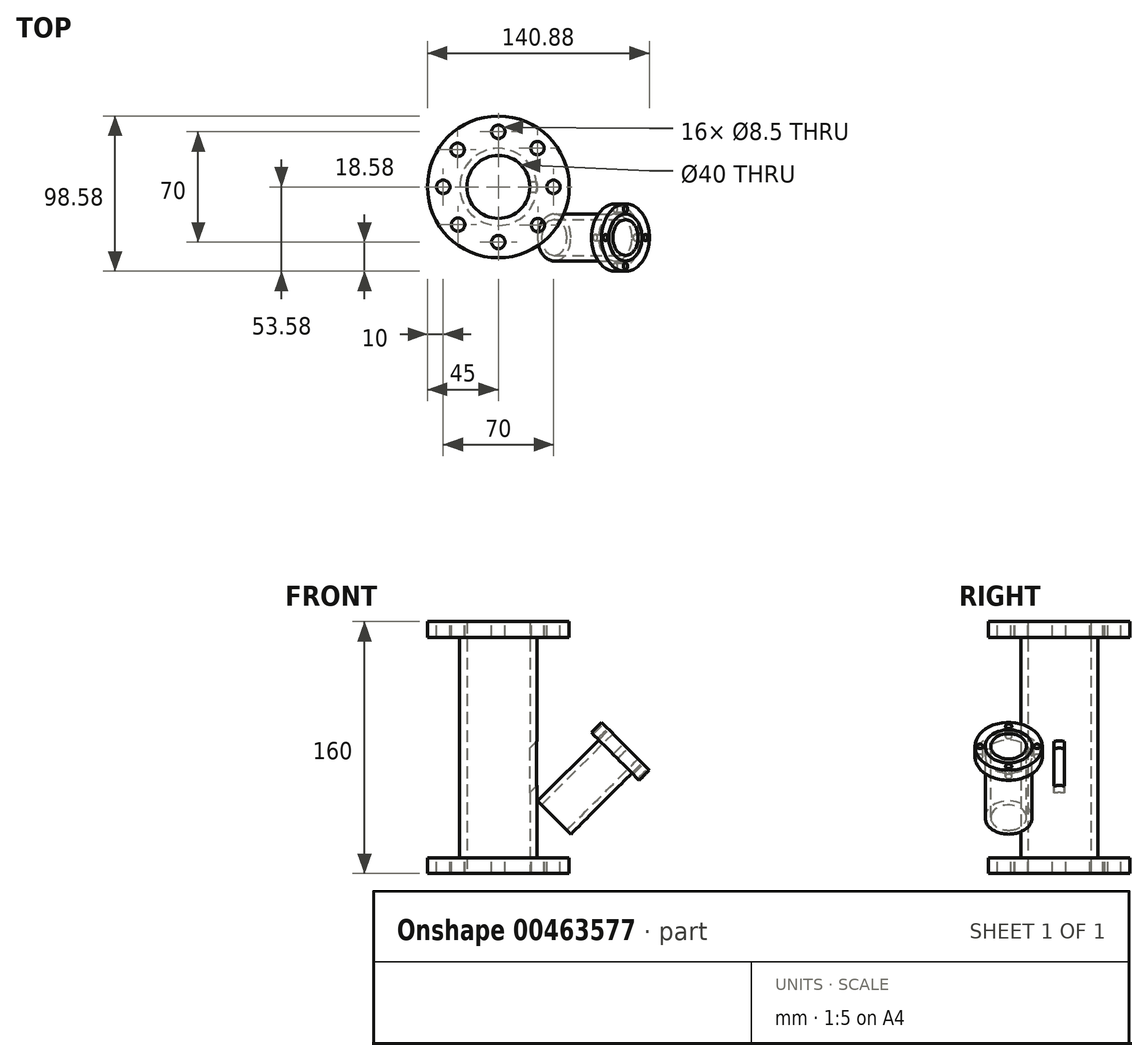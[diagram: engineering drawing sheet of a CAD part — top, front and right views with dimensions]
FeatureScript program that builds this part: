
annotation { "Feature Type Name" : "Feature", "Feature Type Description" : "" }
export const myFeature = defineFeature(function(context is Context, id is Id, definition is map)
    precondition{}
    {
        {
            var Q0;
            Q0=qCreatedBy(makeId("Top.planeOp"),FACE);
            var sketch = newSketch(context, id + "F0", { "sketchPlane" : qUnion([Q0])});
            skCircle(sketch, "E0", {"center": v(0, 0) * mm, "radius": 45 * mm});
            skCircle(sketch, "E1", {"center": v(0, 0) * mm, "radius": 20 * mm});
            skCircle(sketch, "E2", {"center": v(0, 0) * mm, "radius": 24.5 * mm});
            skSolve(sketch);
        }
        {
            var Q0;
            Q0=makeQuery(id+"F0.imprint","IMPRINT",FACE,{"disambiguationData":[TD([[makeQuery(id+"F0.imprint","IMPRINT",EDGE,{"derivedFrom":sQuery(id+"F0.wireOp",EDGE,"E0")}),1.0]])]});
            extrude(context, id + "F1", {"entities" : qUnion([Q0]), "depth" : 10 * mm});
        }
        {
            var Q0;
            Q0=makeQuery(id+"F0.imprint","IMPRINT",FACE,{"disambiguationData":[TD([[makeQuery(id+"F0.imprint","IMPRINT",EDGE,{"derivedFrom":sQuery(id+"F0.wireOp",EDGE,"E1")}),-1.0]])]});
            extrude(context, id + "F2", {"entities" : qUnion([Q0]), "operationType" : NewBodyOperationType.ADD, "depth" : 160 * mm});
        }
        {
            var Q0;
            Q0=makeQuery(id+"F2.opExtrude","CAP_FACE",FACE,{"disambiguationData":[OSD([sQuery(id+"F0.wireOp",EDGE,"E1"),sQuery(id+"F0.wireOp",EDGE,"E2")])],"isStart":false});
            var sketch = newSketch(context, id + "F3", { "sketchPlane" : qUnion([Q0])});
            skCircle(sketch, "E3", {"center": v(0, 0) * mm, "radius": 45 * mm});
            skSolve(sketch);
        }
        {
            var Q0;
            Q0=makeQuery(id+"F3.imprint","IMPRINT",FACE,{"disambiguationData":[TD([[makeQuery(id+"F3.imprint","IMPRINT",EDGE,{"derivedFrom":sQuery(id+"F3.wireOp",EDGE,"E3")}),1.0]])]});
            extrude(context, id + "F4", {"entities" : qUnion([Q0]), "operationType" : NewBodyOperationType.ADD, "oppositeDirection" : true, "depth" : 10 * mm});
        }
        {
            var Q0;
            {var subQ0=sQuery(id+"F0.wireOp",EDGE,"E2");Q0=makeQuery(id+"F4.boolean.opBoolean","MERGE",FACE,{"derivedFrom":[makeQuery(id+"F2.opExtrude","CAP_FACE",FACE,{"disambiguationData":[OSD([sQuery(id+"F0.wireOp",EDGE,"E1"),subQ0])],"isStart":false}),makeQuery(id+"F4.opExtrude","CAP_FACE",FACE,{"disambiguationData":[OSD([subQ0,sQuery(id+"F3.wireOp",EDGE,"E3")])],"isStart":true})]});}
            var sketch = newSketch(context, id + "F5", { "sketchPlane" : qUnion([Q0])});
            skCircle(sketch, "E4", {"center": v(0, 35) * mm, "radius": 4.25 * mm});
            skCircle(sketch, "E5", {"center": v(35, 0) * mm, "radius": 4.25 * mm});
            skCircle(sketch, "E6", {"center": v(0, -35) * mm, "radius": 4.25 * mm});
            skCircle(sketch, "E7", {"center": v(-35, 0) * mm, "radius": 4.25 * mm});
            skCircle(sketch, "E8", {"center": v(-25.85, 23.6) * mm, "radius": 4.25 * mm});
            skCircle(sketch, "E9", {"center": v(24.86, 24.63) * mm, "radius": 4.25 * mm});
            skCircle(sketch, "E10", {"center": v(25.17, -24.32) * mm, "radius": 4.25 * mm});
            skCircle(sketch, "E11", {"center": v(-25.53, -23.94) * mm, "radius": 4.25 * mm});
            skSolve(sketch);
        }
        {
            var Q0;
            Q0=makeQuery(id+"F5.imprint","IMPRINT",FACE,{"disambiguationData":[TD([[makeQuery(id+"F5.imprint","IMPRINT",EDGE,{"derivedFrom":sQuery(id+"F5.wireOp",EDGE,"E8")}),1.0]])]});
            var Q1;
            Q1=makeQuery(id+"F5.imprint","IMPRINT",FACE,{"disambiguationData":[TD([[makeQuery(id+"F5.imprint","IMPRINT",EDGE,{"derivedFrom":sQuery(id+"F5.wireOp",EDGE,"E4")}),1.0]])]});
            var Q2;
            Q2=makeQuery(id+"F5.imprint","IMPRINT",FACE,{"disambiguationData":[TD([[makeQuery(id+"F5.imprint","IMPRINT",EDGE,{"derivedFrom":sQuery(id+"F5.wireOp",EDGE,"E7")}),1.0]])]});
            var Q3;
            Q3=makeQuery(id+"F5.imprint","IMPRINT",FACE,{"disambiguationData":[TD([[makeQuery(id+"F5.imprint","IMPRINT",EDGE,{"derivedFrom":sQuery(id+"F5.wireOp",EDGE,"E11")}),1.0]])]});
            var Q4;
            Q4=makeQuery(id+"F5.imprint","IMPRINT",FACE,{"disambiguationData":[TD([[makeQuery(id+"F5.imprint","IMPRINT",EDGE,{"derivedFrom":sQuery(id+"F5.wireOp",EDGE,"E6")}),1.0]])]});
            var Q5;
            Q5=makeQuery(id+"F5.imprint","IMPRINT",FACE,{"disambiguationData":[TD([[makeQuery(id+"F5.imprint","IMPRINT",EDGE,{"derivedFrom":sQuery(id+"F5.wireOp",EDGE,"E10")}),1.0]])]});
            var Q6;
            Q6=makeQuery(id+"F5.imprint","IMPRINT",FACE,{"disambiguationData":[TD([[makeQuery(id+"F5.imprint","IMPRINT",EDGE,{"derivedFrom":sQuery(id+"F5.wireOp",EDGE,"E5")}),1.0]])]});
            var Q7;
            Q7=makeQuery(id+"F5.imprint","IMPRINT",FACE,{"disambiguationData":[TD([[makeQuery(id+"F5.imprint","IMPRINT",EDGE,{"derivedFrom":sQuery(id+"F5.wireOp",EDGE,"E9")}),1.0]])]});
            extrude(context, id + "F6", {"entities" : qUnion([Q0, Q1, Q2, Q3, Q4, Q5, Q6, Q7]), "operationType" : NewBodyOperationType.REMOVE, "oppositeDirection" : true, "depth" : 177 * mm});
        }
        {
            var Q0;
            Q0=qCreatedBy(makeId("Front.planeOp"),FACE);
            var sketch = newSketch(context, id + "F7", { "sketchPlane" : qUnion([Q0])});
            skLineSegment(sketch, "E12", {"start": v(18.85, 78.47) * mm, "end": v(22.9, 82.51) * mm});
            skLineSegment(sketch, "E13", {"start": v(18.85, 78.47) * mm, "end": v(50.93, 110.55) * mm});
            skLineSegment(sketch, "E14", {"start": v(50.93, 110.55) * mm, "end": v(65.07, 96.41) * mm});
            skLineSegment(sketch, "E15", {"start": v(65.07, 96.41) * mm, "end": v(18.85, 50.19) * mm});
            skLineSegment(sketch, "E16", {"start": v(18.85, 50.19) * mm, "end": v(18.85, 78.47) * mm});
            skPoint(sketch, "E17.end.orphan", {"position": v(22.9, 59.62) * mm});
            skSolve(sketch);
        }
        {
            var Q0;
            {var subQ2=sQuery(id+"F7.wireOp",EDGE,"E14");Q0=makeQuery(id+"F7.imprint","IMPRINT",FACE,{"disambiguationData":[TD([[makeQuery(id+"F7.imprint","IMPRINT",EDGE,{"derivedFrom":subQ2}),-1.0]])]});}
            extrude(context, id + "F8", {"entities" : qUnion([Q0]), "operationType" : NewBodyOperationType.ADD, "endBound" : BoundingType.SYMMETRIC, "depth" : 6.8 * mm});
        }
        {
            var Q0;
            Q0=makeQuery(id+"F8.opExtrude","SWEPT_FACE",FACE,{"disambiguationData":[OSD([sQuery(id+"F7.wireOp",EDGE,"E14")])]});
            var sketch = newSketch(context, id + "F9", { "sketchPlane" : qUnion([Q0])});
            skCircle(sketch, "E18", {"center": v(-32.16, 0) * mm, "radius": 14.9 * mm});
            skPoint(sketch, "E18.centerSnap0", {"position": v(-32.16, -3.4) * mm});
            skCircle(sketch, "E19", {"center": v(-32.16, 0) * mm, "radius": 11.35 * mm});
            skCircle(sketch, "E20", {"center": v(-32.16, 0) * mm, "radius": 21.42 * mm});
            skSolve(sketch);
        }
        {
            var Q0;
            Q0=makeQuery(id+"F9.imprint","IMPRINT",FACE,{"disambiguationData":[TD([[makeQuery(id+"F9.imprint","IMPRINT",EDGE,{"derivedFrom":sQuery(id+"F9.wireOp",EDGE,"E18")}),1.0]])]});
            extrude(context, id + "F10", {"entities" : qUnion([Q0]), "operationType" : NewBodyOperationType.ADD, "oppositeDirection" : true, "depth" : 64 * mm});
        }
        {
            var Q0;
            Q0=makeQuery(id+"F9.imprint","IMPRINT",FACE,{"disambiguationData":[TD([[makeQuery(id+"F9.imprint","IMPRINT",EDGE,{"derivedFrom":sQuery(id+"F9.wireOp",EDGE,"E19")}),1.0]])]});
            var Q1;
            {var subQ0=sQuery(id+"F7.wireOp",EDGE,"E14");Q1=makeQuery(id+"F9.imprint","IMPRINT",FACE,{"disambiguationData":[TD([[makeQuery(id+"F9.imprint","IMPRINT",EDGE,{"derivedFrom":makeQuery(id+"F8.opExtrude","CAP_EDGE",EDGE,{"disambiguationData":[OSD([subQ0])],"isStart":true})}),-1.0]])]});}
            extrude(context, id + "F11", {"entities" : qUnion([Q0, Q1]), "operationType" : NewBodyOperationType.REMOVE, "oppositeDirection" : true, "depth" : 76.1 * mm});
        }
        {
            var Q0;
            Q0=makeQuery(id+"F9.imprint","IMPRINT",FACE,{"disambiguationData":[TD([[makeQuery(id+"F9.imprint","IMPRINT",EDGE,{"derivedFrom":sQuery(id+"F9.wireOp",EDGE,"E18")}),-1.0]])]});
            extrude(context, id + "F12", {"entities" : qUnion([Q0]), "oppositeDirection" : true, "depth" : 9.1 * mm});
        }
        {
            var Q0;
            Q0=makeQuery(id+"F12.opExtrude","CAP_FACE",FACE,{"disambiguationData":[OSD([sQuery(id+"F9.wireOp",EDGE,"E18"),sQuery(id+"F9.wireOp",EDGE,"E20")])],"isStart":true});
            var sketch = newSketch(context, id + "F13", { "sketchPlane" : qUnion([Q0])});
            skCircle(sketch, "E21", {"center": v(-14.03, 0) * mm, "radius": 2 * mm});
            skCircle(sketch, "E22", {"center": v(-32.15, 17.98) * mm, "radius": 2 * mm});
            skCircle(sketch, "E23", {"center": v(-50.36, 0) * mm, "radius": 2 * mm});
            skCircle(sketch, "E24", {"center": v(-32.15, -17.97) * mm, "radius": 2 * mm});
            skSolve(sketch);
        }
        {
            var Q0;
            Q0=makeQuery(id+"F13.imprint","IMPRINT",FACE,{"disambiguationData":[TD([[makeQuery(id+"F13.imprint","IMPRINT",EDGE,{"derivedFrom":sQuery(id+"F13.wireOp",EDGE,"E22")}),1.0]])]});
            var Q1;
            Q1=makeQuery(id+"F13.imprint","IMPRINT",FACE,{"disambiguationData":[TD([[makeQuery(id+"F13.imprint","IMPRINT",EDGE,{"derivedFrom":sQuery(id+"F13.wireOp",EDGE,"E23")}),1.0]])]});
            var Q2;
            Q2=makeQuery(id+"F13.imprint","IMPRINT",FACE,{"disambiguationData":[TD([[makeQuery(id+"F13.imprint","IMPRINT",EDGE,{"derivedFrom":sQuery(id+"F13.wireOp",EDGE,"E24")}),1.0]])]});
            var Q3;
            Q3=makeQuery(id+"F13.imprint","IMPRINT",FACE,{"disambiguationData":[TD([[makeQuery(id+"F13.imprint","IMPRINT",EDGE,{"derivedFrom":sQuery(id+"F13.wireOp",EDGE,"E21")}),1.0]])]});
            extrude(context, id + "F14", {"entities" : qUnion([Q0, Q1, Q2, Q3]), "operationType" : NewBodyOperationType.REMOVE, "oppositeDirection" : true, "depth" : 25 * mm});
        }
        {
            var Q0;
            Q0=qCreatedBy(makeId("Top.planeOp"),FACE);
            var sketch = newSketch(context, id + "F15", { "sketchPlane" : qUnion([Q0])});
            skCircle(sketch, "E25", {"center": v(0, 0) * mm, "radius": 20 * mm});
            skSolve(sketch);
        }
        {
            var Q0;
            Q0=makeQuery(id+"F15.imprint","IMPRINT",FACE,{"disambiguationData":[TD([[makeQuery(id+"F15.imprint","IMPRINT",EDGE,{"derivedFrom":sQuery(id+"F15.wireOp",EDGE,"E25")}),1.0]])]});
            extrude(context, id + "F16", {"entities" : qUnion([Q0]), "operationType" : NewBodyOperationType.REMOVE, "depth" : 171 * mm});
        }
    });
